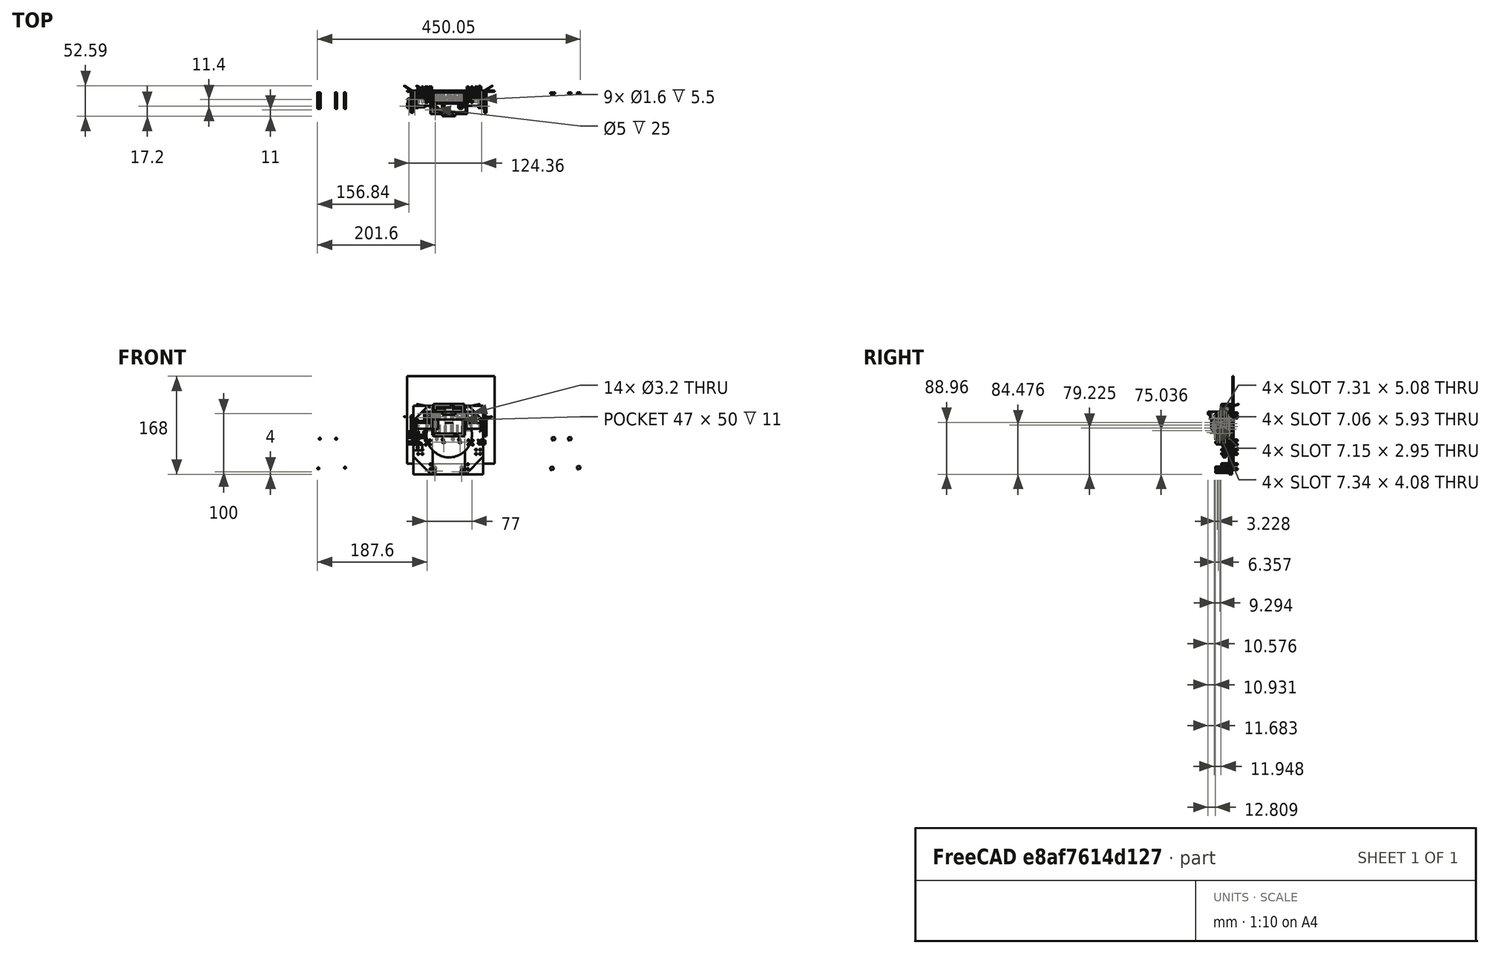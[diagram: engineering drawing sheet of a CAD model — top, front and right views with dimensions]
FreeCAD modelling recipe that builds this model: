
FCSTD DOCUMENT  (FreeCAD 0.17R13522 (Git))
Label: 5028.7 Blank Frank
License: All rights reserved
LicenseURL: http://en.wikipedia.org/wiki/All_rights_reserved
objects: Part::Cylinder×133, Part::Box×78, Part::Fuse×69, Part::Cut×66, Part::Feature×37, Part::MultiFuse×31, Part::Fillet×15, Part::Mirroring×14, Part::Chamfer×10, Part::Cone×9, Part::Compound×3, Part::Torus×2, App::DocumentObjectGroup×1
note: 467 computed .brp shape members not serialized (recipe doc carries the construction recipe); baked Part::Feature solids carry a one-line shape summary decoded from their .brp

FEATURE [Part::Cylinder] Cylinder
  Angle = 360
  AttacherType = Attacher::AttachEngine3D
  Height = 30
  Radius = 7
FEATURE [Part::Cylinder] Cylinder001
  Angle = 360
  AttacherType = Attacher::AttachEngine3D
  Height = 19
  Placement = pos=(0,0,30) rot=(0,0,1;0rad)
  Radius = 7
FEATURE [Part::Cylinder] Cylinder002
  Angle = 360
  AttacherType = Attacher::AttachEngine3D
  Height = 1.8
  Placement = pos=(0,0,49) rot=(0,0,1;0rad)
  Radius = 2.5
FEATURE [Part::Compound] Compound
  Links = -> [Cylinder,Cylinder002,Cylinder001]
FEATURE [Part::Cylinder] Cylinder003
  Angle = 360
  AttacherType = Attacher::AttachEngine3D
  Height = 30
  Radius = 7
FEATURE [Part::Cylinder] Cylinder004
  Angle = 360
  AttacherType = Attacher::AttachEngine3D
  Height = 19
  Placement = pos=(0,0,30) rot=(0,0,1;0rad)
  Radius = 7
FEATURE [Part::Cylinder] Cylinder005
  Angle = 360
  AttacherType = Attacher::AttachEngine3D
  Height = 1.8
  Placement = pos=(0,0,49) rot=(0,0,1;0rad)
  Radius = 2.5
FEATURE [Part::Compound] Compound001
  Links = -> [Cylinder003,Cylinder005,Cylinder004]
  Placement = pos=(14.5,0,50) rot=(1,0,0;3.14159rad)
FEATURE [Part::Cylinder] Cylinder006
  Angle = 360
  AttacherType = Attacher::AttachEngine3D
  Height = 30
  Radius = 7
FEATURE [Part::Cylinder] Cylinder007
  Angle = 360
  AttacherType = Attacher::AttachEngine3D
  Height = 19
  Placement = pos=(0,0,30) rot=(0,0,1;0rad)
  Radius = 7
FEATURE [Part::Cylinder] Cylinder008
  Angle = 360
  AttacherType = Attacher::AttachEngine3D
  Height = 1.8
  Placement = pos=(0,0,49) rot=(0,0,1;0rad)
  Radius = 2.5
FEATURE [Part::Compound] Compound002
  Links = -> [Cylinder006,Cylinder008,Cylinder007]
  Placement = pos=(29,0,0) rot=(0,0,1;0rad)
FEATURE [Part::Box] Box  label="Cube"
  AttacherType = Attacher::AttachEngine3D
  Height = 50
  Length = 47
  Placement = pos=(-9,-8,0) rot=(0,0,1;0rad)
  Width = 12
FEATURE [Part::Box] Box001  label="Cube001"
  AttacherType = Attacher::AttachEngine3D
  Height = 55
  Length = 53
  Placement = pos=(-12,-8,-2.5) rot=(0,0,1;0rad)
  Width = 11
FEATURE [Part::Cylinder] Cylinder009
  Angle = 360
  AttacherType = Attacher::AttachEngine3D
  Height = 50
  Radius = 7
FEATURE [Part::Cylinder] Cylinder010
  Angle = 360
  AttacherType = Attacher::AttachEngine3D
  Height = 50
  Placement = pos=(14.5,0,0) rot=(0,0,1;0rad)
  Radius = 7
FEATURE [Part::Cut] Cut
  Base = -> Box001
  Tool = -> Box
FEATURE [Part::Box] Box002  label="Cube002"
  AttacherType = Attacher::AttachEngine3D
  Height = 55
  Length = 53
  Placement = pos=(-12,3,-2.5) rot=(0,0,1;0rad)
  Width = 7
FEATURE [Part::Fuse] Fusion
  Base = -> Cut
  Tool = -> Box002
FEATURE [Part::Cut] Cut001  label="No idea why this is here...."
  Base = -> Fusion
  Tool = -> Cylinder009
FEATURE [Part::Cylinder] Cylinder011
  Angle = 360
  AttacherType = Attacher::AttachEngine3D
  Height = 50
  Placement = pos=(29,0,0) rot=(0,0,1;0rad)
  Radius = 7
FEATURE [Part::Box] Box003  label="Cube003"
  AttacherType = Attacher::AttachEngine3D
  Height = 5
  Length = 2
  Placement = pos=(28,-9,-2) rot=(0,0,1;0rad)
  Width = 12
FEATURE [Part::Box] Box004  label="Cube004"
  AttacherType = Attacher::AttachEngine3D
  Height = 5
  Length = 2
  Placement = pos=(18.5,-9,46) rot=(0,0,1;0rad)
  Width = 12
FEATURE [Part::Box] Box005  label="Cube005"
  AttacherType = Attacher::AttachEngine3D
  Height = 5
  Length = 2
  Placement = pos=(-2,-9,46) rot=(0,0,1;0rad)
  Width = 12
FEATURE [Part::Box] Box006  label="Cube006"
  AttacherType = Attacher::AttachEngine3D
  Height = 5
  Length = 3
  Placement = pos=(35,-9,-4) rot=(0,0,1;0rad)
  Width = 12
FEATURE [Part::Cut] Cut008
FEATURE [Part::Torus] Torus001
  Angle1 = -180
  Angle2 = 180
  Angle3 = 360
  AttacherType = Attacher::AttachEngine3D
  Placement = pos=(0,0,2) rot=(0,0,1;0rad)
  Radius1 = 19
  Radius2 = 1.5
FEATURE [Part::Cut] Cut009  label="wheel2"
  Base = -> Cut008
  Placement = pos=(75,-7,15) rot=(0,1,0;1.5708rad)
  Tool = -> Torus001
FEATURE [Part::Torus] Torus
  Angle1 = -180
  Angle2 = 180
  Angle3 = 360
  AttacherType = Attacher::AttachEngine3D
  Placement = pos=(0,0,2) rot=(0,0,1;0rad)
  Radius1 = 19
  Radius2 = 1.5
FEATURE [Part::Cut] Cut010
FEATURE [Part::Cut] Cut011  label="wheel1"
  Base = -> Cut010
  Placement = pos=(-51,-7,15) rot=(0,1,0;1.5708rad)
  Tool = -> Torus
FEATURE [Part::Fuse] Fusion003
FEATURE [Part::Cylinder] Cylinder012
  Angle = 360
  AttacherType = Attacher::AttachEngine3D
  Height = 10
  Placement = pos=(5,-4.5,0) rot=(0,1,0;1.5708rad)
  Radius = 0.8
FEATURE [Part::Fuse] Fusion048  label="right-motor001"
  Base = -> Cylinder012
  Placement = pos=(-51,-7,15) rot=(0,0,1;0rad)
  Tool = -> Fusion003
FEATURE [Part::Fuse] Fusion049
FEATURE [Part::Cylinder] Cylinder013
  Angle = 360
  AttacherType = Attacher::AttachEngine3D
  Height = 10
  Placement = pos=(5,-4.5,0) rot=(0,1,0;1.5708rad)
  Radius = 0.8
FEATURE [Part::Fuse] Fusion050  label="left-motor001"
  Base = -> Cylinder013
  Placement = pos=(79,-7,15) rot=(0,0,1;3.14159rad)
  Tool = -> Fusion049
FEATURE [Part::Box] Box007  label="Cube007"
  AttacherType = Attacher::AttachEngine3D
  Height = 5
  Length = 2
  Placement = pos=(37.5,-9,46) rot=(0,0,1;0rad)
  Width = 12
FEATURE [Part::Box] Box008  label="Cube008"
  AttacherType = Attacher::AttachEngine3D
  Height = 5
  Length = 2
  Placement = pos=(8,-9,-2) rot=(0,0,1;0rad)
  Width = 12
FEATURE [Part::Box] Box009  label="The Ground"
  AttacherType = Attacher::AttachEngine3D
  Height = 150
  Length = 150
  Placement = pos=(-57,11,-50) rot=(0,0,1;0rad)
  Width = 2
FEATURE [Part::Box] Box010  label="Motor Mount Left"
  AttacherType = Attacher::AttachEngine3D
  Height = 16
  Length = 4
  Placement = pos=(69,-13,7) rot=(0,0,1;0rad)
  Width = 20
FEATURE [Part::Box] Box011  label="Motor Mount Right"
  AttacherType = Attacher::AttachEngine3D
  Height = 16
  Length = 4
  Placement = pos=(-46,-13,7) rot=(0,0,1;0rad)
  Width = 20
FEATURE [Part::Box] Box012  label="Motor Support Right"
  AttacherType = Attacher::AttachEngine3D
  Height = 16
  Length = 10
  Placement = pos=(-25,-1,7) rot=(0,0,1;0rad)
  Width = 8
FEATURE [Part::Box] Box013  label="Motor Support Left"
  AttacherType = Attacher::AttachEngine3D
  Height = 16
  Length = 10
  Placement = pos=(43,-1,7) rot=(0,0,1;0rad)
  Width = 8
FEATURE [Part::Cylinder] Cylinder014
  Angle = 360
  AttacherType = Attacher::AttachEngine3D
  Height = 28
  Placement = pos=(40.7,0,-10.3) rot=(1,0,0;1.5708rad)
  Radius = 1.6
FEATURE [Part::Cylinder] Cylinder015
  Angle = 360
  AttacherType = Attacher::AttachEngine3D
  Height = 28
  Placement = pos=(-2.4,0,-59.8) rot=(1,0,0;1.5708rad)
  Radius = 1.6
FEATURE [Part::Cylinder] Cylinder016
  Angle = 360
  AttacherType = Attacher::AttachEngine3D
  Height = 28
  Placement = pos=(-5,0,-9) rot=(1,0,0;1.5708rad)
  Radius = 1.6
FEATURE [Part::Cylinder] Cylinder017
  Angle = 360
  AttacherType = Attacher::AttachEngine3D
  Height = 28
  Placement = pos=(25.5,0,-59.8) rot=(1,0,0;1.5708rad)
  Radius = 1.6
FEATURE [Part::Fuse] Fusion051
  Base = -> Cylinder015
  Tool = -> Cylinder016
FEATURE [Part::Fuse] Fusion052
  Base = -> Cylinder014
  Tool = -> Cylinder017
FEATURE [Part::Fuse] Fusion053  label="Screw holes on Arduino Duo"
  Base = -> Fusion051
  Tool = -> Fusion052
FEATURE [Part::Mirroring] Part__Mirroring  label="XXXXXScrew holes on Arduino Duo (Mirror #1)"
  Base = (0,0,0)
  Normal = (0,0,1)
  Placement = pos=(-204,10,-67) rot=(0,0,1;0rad)
  Source = -> Fusion053
FEATURE [Part::Box] Box014  label="Not used Cube"
  AttacherType = Attacher::AttachEngine3D
  Height = 10
  Length = 10
  Placement = pos=(-1,4,-5.85) rot=(0,0,1;0rad)
  Width = 10
FEATURE [Part::Box] Box015  label="Cube014 Arduino Support cube"
  AttacherType = Attacher::AttachEngine3D
  Height = 67
  Length = 55
  Placement = pos=(-13,5,-68) rot=(0,0,1;0rad)
  Width = 5
FEATURE [Part::Cylinder] Cylinder018
  Angle = 360
  AttacherType = Attacher::AttachEngine3D
  Height = 5
  Placement = pos=(15,0,0) rot=(1,0,0;1.5708rad)
  Radius = 39
FEATURE [Part::Cut] Cut014  label="M3 Nut"
  Base = -> Cut001
  Placement = pos=(-6.4,10,-7.2) rot=(1,0,0;1.5708rad)
  Tool = -> Cylinder001
FEATURE [Part::Cut] Cut015  label="M3 Nut001"
  Base = -> Cut001
  Placement = pos=(21.5,10,-7.2) rot=(1,0,0;1.5708rad)
  Tool = -> Cylinder001
FEATURE [Part::Cut] Cut016  label="M3 Nut002"
  Base = -> Cut001
  Placement = pos=(36.7,10,-56.7) rot=(1,0,0;1.5708rad)
  Tool = -> Cylinder001
FEATURE [Part::Cut] Cut017  label="M3 Nut003"
  Base = -> Cut001
  Placement = pos=(-9,10,-58) rot=(1,0,0;1.5708rad)
  Tool = -> Cylinder001
FEATURE [Part::Cut] Cut018
  Base = -> Cut
  Placement = pos=(-9,10,-58) rot=(1,0,0;1.5708rad)
  Tool = -> Box006
FEATURE [Part::Cut] Cut019
  Base = -> Cut
  Placement = pos=(36.7,10,-56.7) rot=(1,0,0;1.5708rad)
  Tool = -> Box006
FEATURE [Part::Cut] Cut020
  Base = -> Cut
  Placement = pos=(-6.4,10,-7.2) rot=(1,0,0;1.5708rad)
  Tool = -> Box006
FEATURE [Part::Cut] Cut021
  Base = -> Cut
  Placement = pos=(21.5,10,-7.2) rot=(1,0,0;1.5708rad)
  Tool = -> Box006
FEATURE [Part::MultiFuse] Fusion054  label="XXXXXHex Holes"
  Placement = pos=(200,0,0) rot=(0,0,1;0rad)
  Shapes = -> [Cut018,Cut021,Cut019,Cut020]
FEATURE [Part::Box] Box016  label="Cube015"
  AttacherType = Attacher::AttachEngine3D
  Height = 117
  Length = 33
  Placement = pos=(-46,7,-68) rot=(0,0,1;0rad)
  Width = 3
FEATURE [Part::Box] Box017  label="Cube016"
  AttacherType = Attacher::AttachEngine3D
  Height = 117
  Length = 31
  Placement = pos=(42,7,-68) rot=(0,0,1;0rad)
  Width = 3
FEATURE [Part::Cylinder] Cylinder019
  Angle = 360
  AttacherType = Attacher::AttachEngine3D
  Height = 28
  Placement = pos=(48,20,-10) rot=(1,0,0;1.5708rad)
  Radius = 1.6
FEATURE [Part::Cylinder] Cylinder020
  Angle = 360
  AttacherType = Attacher::AttachEngine3D
  Height = 28
  Placement = pos=(47,20,-51) rot=(1,0,0;1.5708rad)
  Radius = 1.6
FEATURE [Part::Cylinder] Cylinder021
  Angle = 360
  AttacherType = Attacher::AttachEngine3D
  Height = 28
  Placement = pos=(48,20,-17) rot=(1,0,0;1.5708rad)
  Radius = 1.6
FEATURE [Part::Cylinder] Cylinder022
  Angle = 360
  AttacherType = Attacher::AttachEngine3D
  Height = 28
  Placement = pos=(47,20,-59) rot=(1,0,0;1.5708rad)
  Radius = 1.6
FEATURE [Part::Cylinder] Cylinder023
  Angle = 360
  AttacherType = Attacher::AttachEngine3D
  Height = 28
  Placement = pos=(55,20,-17) rot=(1,0,0;1.5708rad)
  Radius = 1.6
FEATURE [Part::Cylinder] Cylinder024
  Angle = 360
  AttacherType = Attacher::AttachEngine3D
  Height = 28
  Placement = pos=(55,20,-10) rot=(1,0,0;1.5708rad)
  Radius = 1.6
FEATURE [Part::MultiFuse] Fusion055
  Shapes = -> [Cylinder021,Cylinder023,Cylinder024,Cylinder019]
FEATURE [Part::MultiFuse] Fusion056
  Placement = pos=(13,0,-16) rot=(0,0,1;0rad)
  Shapes = -> [Cylinder021,Cylinder023,Cylinder024,Cylinder019]
FEATURE [Part::MultiFuse] Fusion057  label="Mount holes top left"
  Placement = pos=(-1,0,46) rot=(0,0,1;0rad)
  Shapes = -> [Cylinder021,Cylinder023,Cylinder024,Cylinder019]
FEATURE [Part::MultiFuse] Fusion058  label="Mount holes top right"
  Placement = pos=(-71,0,46) rot=(0,0,1;0rad)
  Shapes = -> [Cylinder021,Cylinder023,Cylinder024,Cylinder019]
FEATURE [Part::MultiFuse] Fusion059
  Shapes = -> [Cylinder022,Cylinder020,Fusion055,Fusion056]
FEATURE [Part::Mirroring] Part__Mirroring001  label="Mount holes bottom right"
  Base = (0,0,0)
  Normal = (1,0,0)
  Placement = pos=(30,0,0) rot=(0,0,1;0rad)
  Source = -> Fusion059
FEATURE [Part::Cylinder] Cylinder025
  Angle = 360
  AttacherType = Attacher::AttachEngine3D
  Height = 28
  Placement = pos=(48,20,-10) rot=(1,0,0;1.5708rad)
  Radius = 1.6
FEATURE [Part::Cylinder] Cylinder026
  Angle = 360
  AttacherType = Attacher::AttachEngine3D
  Height = 28
  Placement = pos=(47,20,-51) rot=(1,0,0;1.5708rad)
  Radius = 1.6
FEATURE [Part::Cylinder] Cylinder027
  Angle = 360
  AttacherType = Attacher::AttachEngine3D
  Height = 28
  Placement = pos=(48,20,-17) rot=(1,0,0;1.5708rad)
  Radius = 1.6
FEATURE [Part::Cylinder] Cylinder028
  Angle = 360
  AttacherType = Attacher::AttachEngine3D
  Height = 28
  Placement = pos=(47,20,-59) rot=(1,0,0;1.5708rad)
  Radius = 1.6
FEATURE [Part::Cylinder] Cylinder029
  Angle = 360
  AttacherType = Attacher::AttachEngine3D
  Height = 28
  Placement = pos=(55,20,-17) rot=(1,0,0;1.5708rad)
  Radius = 1.6
FEATURE [Part::Cylinder] Cylinder030
  Angle = 360
  AttacherType = Attacher::AttachEngine3D
  Height = 28
  Placement = pos=(55,20,-10) rot=(1,0,0;1.5708rad)
  Radius = 1.6
FEATURE [Part::MultiFuse] Fusion060
  Shapes = -> [Cylinder027,Cylinder029,Cylinder030,Cylinder025]
FEATURE [Part::MultiFuse] Fusion061
  Placement = pos=(13,0,-16) rot=(0,0,1;0rad)
  Shapes = -> [Cylinder027,Cylinder029,Cylinder030,Cylinder025]
FEATURE [Part::MultiFuse] Fusion062  label="Mount holes bottom left"
  Shapes = -> [Cylinder028,Cylinder026,Fusion060,Fusion061]
FEATURE [Part::Cylinder] Cylinder031  label="Cylinder127"
  Angle = 360
  AttacherType = Attacher::AttachEngine3D
  Height = 10
  Placement = pos=(0,18,29) rot=(0,0,1;0rad)
  Radius = 2.25
FEATURE [Part::Cylinder] Cylinder032  label="Cylinder128"
  Angle = 360
  AttacherType = Attacher::AttachEngine3D
  Height = 10
  Placement = pos=(4.5,18,32) rot=(0,0,1;0rad)
  Radius = 1
FEATURE [Part::Cylinder] Cylinder033  label="Cylinder129"
  Angle = 360
  AttacherType = Attacher::AttachEngine3D
  Height = 10
  Placement = pos=(-4.5,18,32) rot=(0,0,1;0rad)
  Radius = 1
FEATURE [Part::Fuse] Fusion009  label="Mounting Screw Holes"
  Base = -> Cylinder032
  Tool = -> Cylinder033
FEATURE [Part::Fuse] Fusion071  label="Motor Holes Left"
  Base = -> Cylinder031
  Placement = pos=(37,-7,-3) rot=(0.57735,0.57735,0.57735;2.0944rad)
  Tool = -> Fusion009
FEATURE [Part::Cylinder] Cylinder034  label="Cylinder130"
  Angle = 360
  AttacherType = Attacher::AttachEngine3D
  Height = 10
  Placement = pos=(0,18,29) rot=(0,0,1;0rad)
  Radius = 2.25
FEATURE [Part::Cylinder] Cylinder035  label="Cylinder131"
  Angle = 360
  AttacherType = Attacher::AttachEngine3D
  Height = 10
  Placement = pos=(4.5,18,32) rot=(0,0,1;0rad)
  Radius = 1
FEATURE [Part::Cylinder] Cylinder036  label="Cylinder132"
  Angle = 360
  AttacherType = Attacher::AttachEngine3D
  Height = 10
  Placement = pos=(-4.5,18,32) rot=(0,0,1;0rad)
  Radius = 1
FEATURE [Part::Fuse] Fusion072  label="Mounting Screw Holes001"
  Base = -> Cylinder035
  Tool = -> Cylinder036
FEATURE [Part::Fuse] Fusion073  label="Motor Holes Right"
  Base = -> Cylinder034
  Placement = pos=(-79,-7,-3) rot=(0.57735,0.57735,0.57735;2.0944rad)
  Tool = -> Fusion072
FEATURE [Part::Cylinder] Cylinder037  label="Cylinder133"
  Angle = 360
  AttacherType = Attacher::AttachEngine3D
  Height = 28
  Placement = pos=(40.7,0,-10.3) rot=(1,0,0;1.5708rad)
  Radius = 1.6
FEATURE [Part::Cylinder] Cylinder038  label="Cylinder134"
  Angle = 360
  AttacherType = Attacher::AttachEngine3D
  Height = 28
  Placement = pos=(-2.4,0,-59.8) rot=(1,0,0;1.5708rad)
  Radius = 1.6
FEATURE [Part::Cylinder] Cylinder039  label="Cylinder135"
  Angle = 360
  AttacherType = Attacher::AttachEngine3D
  Height = 28
  Placement = pos=(-5,0,-9) rot=(1,0,0;1.5708rad)
  Radius = 1.6
FEATURE [Part::Cylinder] Cylinder040  label="Cylinder136"
  Angle = 360
  AttacherType = Attacher::AttachEngine3D
  Height = 28
  Placement = pos=(25.5,0,-59.8) rot=(1,0,0;1.5708rad)
  Radius = 1.6
FEATURE [Part::Fuse] Fusion074
  Base = -> Cylinder038
  Tool = -> Cylinder039
FEATURE [Part::Fuse] Fusion075
  Base = -> Cylinder037
  Tool = -> Cylinder040
FEATURE [Part::Fuse] Fusion076  label="Screw holes on Arduino Duo001"
  Base = -> Fusion074
  Tool = -> Fusion075
FEATURE [Part::Mirroring] Part__Mirroring002  label="Screw holes on Arduino Duo (Mirror #1)001"
  Base = (0,0,0)
  Normal = (0,0,1)
  Placement = pos=(-4,10,-67) rot=(0,0,1;0rad)
  Source = -> Fusion076
FEATURE [Part::Mirroring] Part__Mirroring003  label="Screw holes on Arduino Duo (Mirror #1)001 (Mirror #4)"
  Base = (0,0,0)
  Normal = (1,0,0)
  Placement = pos=(27,0,-6) rot=(0,0,1;0rad)
  Source = -> Part__Mirroring002
FEATURE [Part::Box] Box018  label="Cube017"
  AttacherType = Attacher::AttachEngine3D
  Height = 50
  Length = 47
  Placement = pos=(-9,-8,0) rot=(0,0,1;0rad)
  Width = 12
FEATURE [Part::Box] Box019  label="Cube018"
  AttacherType = Attacher::AttachEngine3D
  Height = 55
  Length = 53
  Placement = pos=(-12,-8,-2.5) rot=(0,0,1;0rad)
  Width = 11
FEATURE [Part::Cut] Cut031
  Base = -> Box019
  Tool = -> Box018
FEATURE [Part::Box] Box020  label="Cube019"
  AttacherType = Attacher::AttachEngine3D
  Height = 5
  Length = 3
  Placement = pos=(35,-9,-4) rot=(0,0,1;0rad)
  Width = 12
FEATURE [Part::Cut] Cut032
  Base = -> Cut031
  Placement = pos=(-9,10,-58) rot=(1,0,0;1.5708rad)
  Tool = -> Box020
FEATURE [Part::Cut] Cut033
  Base = -> Cut031
  Placement = pos=(36.7,10,-56.7) rot=(1,0,0;1.5708rad)
  Tool = -> Box020
FEATURE [Part::Cut] Cut034
  Base = -> Cut031
  Placement = pos=(-6.4,10,-7.2) rot=(1,0,0;1.5708rad)
  Tool = -> Box020
FEATURE [Part::Cut] Cut035
  Base = -> Cut031
  Placement = pos=(21.5,10,-7.2) rot=(1,0,0;1.5708rad)
  Tool = -> Box020
FEATURE [Part::MultiFuse] Fusion077
  Shapes = -> [Cut032,Cut035,Cut033,Cut034]
FEATURE [Part::Mirroring] Part__Mirroring004  label="Hex Holes"
  Base = (0,0,0)
  Normal = (1,0,0)
  Placement = pos=(27,0,-6) rot=(0,0,1;0rad)
  Source = -> Fusion077
FEATURE [Part::Box] Box021  label="Cube020"
  AttacherType = Attacher::AttachEngine3D
  Height = 13
  Length = 63
  Placement = pos=(-17,-27,26) rot=(0,0,1;0rad)
  Width = 34
FEATURE [Part::Box] Box022  label="Cube021"
  AttacherType = Attacher::AttachEngine3D
  Height = 13
  Length = 12
  Placement = pos=(45,4,26) rot=(0,0,1;0rad)
  Width = 3
FEATURE [Part::Box] Box023  label="Cube022"
  AttacherType = Attacher::AttachEngine3D
  Height = 13
  Length = 12
  Placement = pos=(-28,4,26) rot=(0,0,1;0rad)
  Width = 3
FEATURE [Part::Box] Box024  label="Cube023"
  AttacherType = Attacher::AttachEngine3D
  Height = 13
  Length = 57
  Placement = pos=(-14,-24,26) rot=(0,0,1;0rad)
  Width = 31
FEATURE [Part::Cylinder] Cylinder041  label="Cylinder137"
  Angle = 360
  AttacherType = Attacher::AttachEngine3D
  Height = 28
  Placement = pos=(54,20,29) rot=(1,0,0;1.5708rad)
  Radius = 1.6
FEATURE [Part::Cylinder] Cylinder042  label="Cylinder138"
  Angle = 360
  AttacherType = Attacher::AttachEngine3D
  Height = 28
  Placement = pos=(54,20,36) rot=(1,0,0;1.5708rad)
  Radius = 1.6
FEATURE [Part::Cylinder] Cylinder043  label="Cylinder139"
  Angle = 360
  AttacherType = Attacher::AttachEngine3D
  Height = 28
  Placement = pos=(-23,20,29) rot=(1,0,0;1.5708rad)
  Radius = 1.6
FEATURE [Part::Cylinder] Cylinder044  label="Cylinder140"
  Angle = 360
  AttacherType = Attacher::AttachEngine3D
  Height = 28
  Placement = pos=(-23,20,36) rot=(1,0,0;1.5708rad)
  Radius = 1.6
FEATURE [Part::Cylinder] Cylinder045  label="Cylinder141"
  Angle = 360
  AttacherType = Attacher::AttachEngine3D
  Height = 10
  Placement = pos=(36,-17.25,32.5) rot=(0,1,0;1.5708rad)
  Radius = 2.5
FEATURE [Part::Cut] Cut037
  Base = -> Box021
  Tool = -> Box024
FEATURE [Part::Cut] Cut038
  Base = -> Cut037
  Tool = -> Cylinder045
FEATURE [Part::Box] Box025  label="Cube024"
  AttacherType = Attacher::AttachEngine3D
  Height = 5
  Length = 22
  Placement = pos=(3.5,-31,34) rot=(0,0,1;0rad)
  Width = 4
FEATURE [Part::Cylinder] Cylinder046  label="Cylinder142"
  Angle = 360
  AttacherType = Attacher::AttachEngine3D
  Height = 10
  Placement = pos=(20.75,-29,30) rot=(0,0,1;0rad)
  Radius = 0.85
FEATURE [Part::Cylinder] Cylinder047  label="Cylinder143"
  Angle = 360
  AttacherType = Attacher::AttachEngine3D
  Height = 10
  Placement = pos=(8.25,-29,40) rot=(1,0,0;3.14159rad)
  Radius = 0.85
FEATURE [Part::Fuse] Fusion078
  Base = -> Cylinder046
  Tool = -> Cylinder047
FEATURE [Part::Cut] Cut039
  Base = -> Box025
  Tool = -> Fusion078
FEATURE [Part::Fuse] Fusion079
  Base = -> Cut038
  Tool = -> Cut039
FEATURE [Part::Fuse] Fusion080
  Base = -> Cylinder043
  Tool = -> Cylinder044
FEATURE [Part::Fuse] Fusion081
  Base = -> Cylinder041
  Tool = -> Cylinder042
FEATURE [Part::Fuse] Fusion082
  Base = -> Box023
  Tool = -> Fusion079
FEATURE [Part::Fuse] Fusion083
  Base = -> Box022
  Tool = -> Fusion082
FEATURE [Part::Cut] Cut040
  Base = -> Fusion083
  Tool = -> Fusion081
FEATURE [Part::Cut] Cut041  label="Switch Bracket"
  Base = -> Cut040
  Tool = -> Fusion080
FEATURE [Part::Cylinder] Cylinder048  label="Cylinder144"
  Angle = 360
  AttacherType = Attacher::AttachEngine3D
  Height = 28
  Placement = pos=(-23,20,29) rot=(1,0,0;1.5708rad)
  Radius = 1.6
FEATURE [Part::Cylinder] Cylinder049  label="Cylinder145"
  Angle = 360
  AttacherType = Attacher::AttachEngine3D
  Height = 28
  Placement = pos=(-23,20,36) rot=(1,0,0;1.5708rad)
  Radius = 1.6
FEATURE [Part::Fuse] Fusion084
  Base = -> Cylinder048
  Placement = pos=(1,0,0) rot=(0,0,1;0rad)
  Tool = -> Cylinder049
FEATURE [Part::Cylinder] Cylinder050  label="Cylinder146"
  Angle = 360
  AttacherType = Attacher::AttachEngine3D
  Height = 28
  Placement = pos=(-23,20,29) rot=(1,0,0;1.5708rad)
  Radius = 1.6
FEATURE [Part::Cylinder] Cylinder051  label="Cylinder147"
  Angle = 360
  AttacherType = Attacher::AttachEngine3D
  Height = 28
  Placement = pos=(-23,20,36) rot=(1,0,0;1.5708rad)
  Radius = 1.6
FEATURE [Part::Fuse] Fusion085
  Base = -> Cylinder050
  Placement = pos=(-1,0,0) rot=(0,0,1;0rad)
  Tool = -> Cylinder051
FEATURE [Part::Cut] Cut042
  Base = -> Cut041
  Tool = -> Fusion084
FEATURE [Part::Cut] Cut043  label="Switch Bracket001"
  Base = -> Cut042
  Tool = -> Fusion085
FEATURE [Part::Cylinder] Cylinder052  label="Cylinder148"
  Angle = 360
  AttacherType = Attacher::AttachEngine3D
  Height = 42
  Radius = 5.15
FEATURE [Part::Cylinder] Cylinder053  label="Cylinder149"
  Angle = 360
  AttacherType = Attacher::AttachEngine3D
  Height = 1.6
  Placement = pos=(0,0,42) rot=(0,0,1;0rad)
  Radius = 1.65
FEATURE [Part::Fuse] Fusion086
  Base = -> Cylinder052
  Placement = pos=(2,0,0) rot=(0,0,1;0rad)
  Tool = -> Cylinder053
FEATURE [Part::Cylinder] Cylinder054  label="Cylinder150"
  Angle = 360
  AttacherType = Attacher::AttachEngine3D
  Height = 42
  Radius = 4.8
FEATURE [Part::Cylinder] Cylinder055  label="Cylinder151"
  Angle = 360
  AttacherType = Attacher::AttachEngine3D
  Height = 1.6
  Placement = pos=(0,0,42) rot=(0,0,1;0rad)
  Radius = 1.65
FEATURE [Part::Fuse] Fusion087
  Base = -> Cylinder054
  Placement = pos=(12,0,0) rot=(0,0,1;0rad)
  Tool = -> Cylinder055
FEATURE [Part::Cylinder] Cylinder056  label="Cylinder152"
  Angle = 360
  AttacherType = Attacher::AttachEngine3D
  Height = 42
  Radius = 4.8
FEATURE [Part::Cylinder] Cylinder057  label="Cylinder153"
  Angle = 360
  AttacherType = Attacher::AttachEngine3D
  Height = 1.6
  Placement = pos=(0,0,42) rot=(0,0,1;0rad)
  Radius = 1.65
FEATURE [Part::Fuse] Fusion088
  Base = -> Cylinder056
  Placement = pos=(22,0,0) rot=(0,0,1;0rad)
  Tool = -> Cylinder057
FEATURE [Part::Cylinder] Cylinder058  label="Cylinder154"
  Angle = 360
  AttacherType = Attacher::AttachEngine3D
  Height = 42
  Radius = 4.8
FEATURE [Part::Cylinder] Cylinder059  label="Cylinder155"
  Angle = 360
  AttacherType = Attacher::AttachEngine3D
  Height = 1.6
  Placement = pos=(0,0,42) rot=(0,0,1;0rad)
  Radius = 1.65
FEATURE [Part::Fuse] Fusion089
  Base = -> Cylinder058
  Placement = pos=(32,0,0) rot=(0,0,1;0rad)
  Tool = -> Cylinder059
FEATURE [Part::Cylinder] Cylinder060  label="Cylinder156"
  Angle = 360
  AttacherType = Attacher::AttachEngine3D
  Height = 42
  Radius = 5.15
FEATURE [Part::Cylinder] Cylinder061  label="Cylinder157"
  Angle = 360
  AttacherType = Attacher::AttachEngine3D
  Height = 1.6
  Placement = pos=(0,0,42) rot=(0,0,1;0rad)
  Radius = 1.65
FEATURE [Part::Fuse] Fusion093
  Base = -> Cylinder060
  Placement = pos=(-8,0,0) rot=(0,0,1;0rad)
  Tool = -> Cylinder061
FEATURE [Part::MultiFuse] Fusion094  label="AAA Batts"
  Placement = pos=(2.5,0,2) rot=(0,0,1;0rad)
  Shapes = -> [Fusion093,Fusion086,Fusion087,Fusion088,Fusion089]
FEATURE [Part::Cylinder] Cylinder062  label="Cylinder158"
  Angle = 360
  AttacherType = Attacher::AttachEngine3D
  Height = 10
  Radius = 17
FEATURE [Part::Cylinder] Cylinder063  label="Cylinder159"
  Angle = 360
  AttacherType = Attacher::AttachEngine3D
  Height = 16
  Placement = pos=(0,0,-4) rot=(0,0,1;0rad)
  Radius = 10
FEATURE [Part::Cut] Cut044
  Base = -> Cylinder062
  Tool = -> Cylinder063
FEATURE [Part::Box] Box026  label="Cube025"
  AttacherType = Attacher::AttachEngine3D
  Height = 20
  Length = 18
  Placement = pos=(0,0,-5) rot=(0,0,1;0rad)
  Width = 20
FEATURE [Part::Box] Box027  label="Cube026"
  AttacherType = Attacher::AttachEngine3D
  Height = 20
  Length = 10
  Placement = pos=(0,0,-5) rot=(0,0,1;0.174533rad)
  Width = 20
FEATURE [Part::Cut] Cut045
  Base = -> Box027
  Tool = -> Box026
FEATURE [Part::Feature] Cut045001
  Placement = pos=(0,0,0) rot=(0,0,1;0.349066rad)
  shape: bbox 10 x 22.32 x 20 mm, 7 faces (baked)
FEATURE [Part::Feature] Cut045002
  Placement = pos=(0,0,0) rot=(0,0,1;0.698132rad)
  shape: bbox 15.32 x 20.52 x 20 mm, 7 faces (baked)
FEATURE [Part::Feature] Cut045003
  Placement = pos=(0,0,0) rot=(0,0,1;1.0472rad)
  shape: bbox 18.79 x 16.24 x 20 mm, 7 faces (baked)
FEATURE [Part::Feature] Cut045004
  Placement = pos=(0,0,0) rot=(0,0,1;1.39626rad)
  shape: bbox 20 x 10 x 20 mm, 7 faces (baked)
FEATURE [Part::Feature] Cut045005
  Placement = pos=(0,0,0) rot=(0,0,1;1.74533rad)
  shape: bbox 22.21 x 9.894 x 20 mm, 7 faces (baked)
FEATURE [Part::Feature] Cut045006
  Placement = pos=(0,0,0) rot=(0,0,1;2.0944rad)
  shape: bbox 21.75 x 12.86 x 20 mm, 7 faces (baked)
FEATURE [Part::Feature] Cut045007
  Placement = pos=(0,0,0) rot=(0,0,1;2.44346rad)
  shape: bbox 18.66 x 17.32 x 20 mm, 7 faces (baked)
FEATURE [Part::Feature] Cut045008
  Placement = pos=(0,0,0) rot=(0,0,1;2.79253rad)
  shape: bbox 13.32 x 19.7 x 20 mm, 7 faces (baked)
FEATURE [Part::Feature] Cut045009
  Placement = pos=(0,0,0) rot=(0,0,1;3.14159rad)
  shape: bbox 10.1 x 21.43 x 20 mm, 7 faces (baked)
FEATURE [Part::Feature] Cut045010
  Placement = pos=(0,0,0) rot=(0,0,1;3.49066rad)
  shape: bbox 10 x 22.32 x 20 mm, 7 faces (baked)
FEATURE [Part::Feature] Cut045011
  Placement = pos=(0,0,0) rot=(0,0,1;3.83972rad)
  shape: bbox 15.32 x 20.52 x 20 mm, 7 faces (baked)
FEATURE [Part::Feature] Cut045012
  Placement = pos=(0,0,0) rot=(0,0,1;4.18879rad)
  shape: bbox 18.79 x 16.24 x 20 mm, 7 faces (baked)
FEATURE [Part::Feature] Cut045013
  Placement = pos=(0,0,0) rot=(0,0,-1;1.74533rad)
  shape: bbox 20 x 10 x 20 mm, 7 faces (baked)
FEATURE [Part::Feature] Cut045014
  Placement = pos=(0,0,0) rot=(0,0,-1;1.39626rad)
  shape: bbox 22.21 x 9.894 x 20 mm, 7 faces (baked)
FEATURE [Part::Feature] Cut045015
  Placement = pos=(0,0,0) rot=(0,0,-1;1.0472rad)
  shape: bbox 21.75 x 12.86 x 20 mm, 7 faces (baked)
FEATURE [Part::Feature] Cut045016
  Placement = pos=(0,0,0) rot=(0,0,-1;0.698132rad)
  shape: bbox 18.66 x 17.32 x 20 mm, 7 faces (baked)
FEATURE [Part::Feature] Cut045017
  Placement = pos=(0,0,0) rot=(0,0,-1;0.349066rad)
  shape: bbox 13.32 x 19.7 x 20 mm, 7 faces (baked)
FEATURE [Part::MultiFuse] Fusion095
  Shapes = -> [Cut045001,Cut045008,Cut045010,Cut045009,Cut045005,Cut045003,Cut045006,Cut045002,Cut045004,Cut045007,Cut045016,Cut045017,Cut045011,Cut045012,Cut045013,Cut045014,Cut045015,Cut045]
FEATURE [Part::Cut] Cut045018
  Base = -> Cut044
  Placement = pos=(72,-7,15) rot=(0,1,0;1.5708rad)
  Tool = -> Fusion095
FEATURE [Part::Cut] Cut045019  label="Wheel with Spokes AB"
  Base = -> Cut009
  Tool = -> Cut045018
FEATURE [Part::Box] Box028  label="Cube027"
  AttacherType = Attacher::AttachEngine3D
  Height = 5
  Length = 2
  Placement = pos=(37.5,-9,-2) rot=(0,0,1;0rad)
  Width = 12
FEATURE [Part::Box] Box029  label="Cube028"
  AttacherType = Attacher::AttachEngine3D
  Height = 50
  Length = 47
  Placement = pos=(-9,-8,0) rot=(0,0,1;0rad)
  Width = 12
FEATURE [Part::Box] Box030  label="Cube029"
  AttacherType = Attacher::AttachEngine3D
  Height = 55
  Length = 53
  Placement = pos=(-12,-8,-2.5) rot=(0,0,1;0rad)
  Width = 11
FEATURE [Part::Cylinder] Cylinder064  label="Cylinder160"
  Angle = 360
  AttacherType = Attacher::AttachEngine3D
  Height = 50
  Radius = 7
FEATURE [Part::Cut] Cut045020
  Base = -> Box030
  Tool = -> Box029
FEATURE [Part::Box] Box031  label="Cube030"
  AttacherType = Attacher::AttachEngine3D
  Height = 55
  Length = 53
  Placement = pos=(-12,3,-2.5) rot=(0,0,1;0rad)
  Width = 7
FEATURE [Part::Fuse] Fusion096
  Base = -> Cut045020
  Tool = -> Box031
FEATURE [Part::Box] Box032  label="Battery Base"
  AttacherType = Attacher::AttachEngine3D
  Height = 50
  Length = 56
  Placement = pos=(-14,3,-1) rot=(0,0,1;0rad)
  Width = 7
FEATURE [Part::Box] Box033  label="Cube031"
  AttacherType = Attacher::AttachEngine3D
  Height = 30
  Length = 10
  Placement = pos=(-14,-25,9) rot=(0,0,1;0rad)
  Width = 10
FEATURE [Part::Cylinder] Cylinder065  label="Cylinder161"
  Angle = 360
  AttacherType = Attacher::AttachEngine3D
  Height = 43.5
  Placement = pos=(4,0,2) rot=(0,0,1;0rad)
  Radius = 4.8
FEATURE [Part::Cylinder] Cylinder066  label="Cylinder162"
  Angle = 360
  AttacherType = Attacher::AttachEngine3D
  Height = 1.6
  Placement = pos=(4,0,44) rot=(0,0,1;0rad)
  Radius = 1.65
FEATURE [Part::Fuse] Fusion097
  Base = -> Cylinder065
  Tool = -> Cylinder066
FEATURE [Part::Cylinder] Cylinder067  label="Cylinder163"
  Angle = 360
  AttacherType = Attacher::AttachEngine3D
  Height = 43.5
  Placement = pos=(14,0,2) rot=(0,0,1;0rad)
  Radius = 4.8
FEATURE [Part::Cylinder] Cylinder068  label="Cylinder164"
  Angle = 360
  AttacherType = Attacher::AttachEngine3D
  Height = 1.6
  Placement = pos=(14,0,44) rot=(0,0,1;0rad)
  Radius = 1.65
FEATURE [Part::Fuse] Fusion098
  Base = -> Cylinder067
  Tool = -> Cylinder068
FEATURE [Part::Cylinder] Cylinder069  label="Cylinder165"
  Angle = 360
  AttacherType = Attacher::AttachEngine3D
  Height = 43.5
  Placement = pos=(24,0,2) rot=(0,0,1;0rad)
  Radius = 4.8
FEATURE [Part::Cylinder] Cylinder070  label="Cylinder166"
  Angle = 360
  AttacherType = Attacher::AttachEngine3D
  Height = 1.6
  Placement = pos=(24,0,44) rot=(0,0,1;0rad)
  Radius = 1.65
FEATURE [Part::Fuse] Fusion099
  Base = -> Cylinder069
  Tool = -> Cylinder070
FEATURE [Part::Cylinder] Cylinder071  label="Cylinder167"
  Angle = 360
  AttacherType = Attacher::AttachEngine3D
  Height = 43.5
  Placement = pos=(34,0,2) rot=(0,0,1;0rad)
  Radius = 4.8
FEATURE [Part::Cylinder] Cylinder072  label="Cylinder168"
  Angle = 360
  AttacherType = Attacher::AttachEngine3D
  Height = 1.6
  Placement = pos=(34,0,44) rot=(0,0,1;0rad)
  Radius = 1.65
FEATURE [Part::Fuse] Fusion100
  Base = -> Cylinder071
  Tool = -> Cylinder072
FEATURE [Part::Cylinder] Cylinder073  label="Cylinder169"
  Angle = 360
  AttacherType = Attacher::AttachEngine3D
  Height = 43.5
  Placement = pos=(-6,0,2) rot=(0,0,1;0rad)
  Radius = 4.8
FEATURE [Part::Cylinder] Cylinder074  label="Cylinder170"
  Angle = 360
  AttacherType = Attacher::AttachEngine3D
  Height = 1.6
  Placement = pos=(-6,0,44) rot=(0,0,1;0rad)
  Radius = 1.65
FEATURE [Part::Fuse] Fusion101
  Base = -> Cylinder073
  Tool = -> Cylinder074
FEATURE [Part::MultiFuse] Fusion102  label="AAA Batts001"
  Shapes = -> [Fusion101,Fusion097,Fusion098,Fusion099,Fusion100]
FEATURE [Part::Cylinder] Cylinder075  label="Cylinder171"
  Angle = 360
  AttacherType = Attacher::AttachEngine3D
  Height = 10
  Placement = pos=(-9,-20,4) rot=(0,0,1;0rad)
  Radius = 2.75
FEATURE [Part::Cylinder] Cylinder076  label="Cylinder172"
  Angle = 360
  AttacherType = Attacher::AttachEngine3D
  Height = 27
  Placement = pos=(-9,-20,14) rot=(0,0,1;0rad)
  Radius = 2.5
FEATURE [Part::Fuse] Fusion103  label="phototransistor hole"
  Base = -> Cylinder075
  Tool = -> Cylinder076
FEATURE [Part::Cut] Cut045021  label="Phototransistor holder"
  Base = -> Box033
  Tool = -> Fusion103
FEATURE [Part::Fuse] Fusion104  label="Switch Mount with phototransistor hole"
  Base = -> Cut043
  Tool = -> Cut045021
FEATURE [Part::Cut] Cut045022
  Base = -> Box032
  Tool = -> Fusion102
FEATURE [Part::Box] Box034  label="Cube032"
  AttacherType = Attacher::AttachEngine3D
  Height = 2.5
  Length = 55
  Placement = pos=(-13,-9,-1) rot=(0,0,1;0rad)
  Width = 12
FEATURE [Part::Box] Box035  label="Cube033"
  AttacherType = Attacher::AttachEngine3D
  Height = 2.5
  Length = 55
  Placement = pos=(-13,-9,46.5) rot=(0,0,1;0rad)
  Width = 12
FEATURE [Part::Box] Box036  label="Cube034"
  AttacherType = Attacher::AttachEngine3D
  Height = 50
  Length = 2
  Placement = pos=(-14,-9,-1) rot=(0,0,1;0rad)
  Width = 12
FEATURE [Part::Box] Box037  label="Cube035"
  AttacherType = Attacher::AttachEngine3D
  Height = 50
  Length = 2
  Placement = pos=(40,-9,-1) rot=(0,0,1;0rad)
  Width = 12
FEATURE [Part::MultiFuse] Fusion105
  Shapes = -> [Box034,Box036,Box037,Box035]
FEATURE [Part::Box] Box038  label="Cube036"
  AttacherType = Attacher::AttachEngine3D
  Height = 5
  Length = 2
  Placement = pos=(-10.5,-9,46) rot=(0,0,1;0rad)
  Width = 12
FEATURE [Part::Box] Box039  label="Cube037"
  AttacherType = Attacher::AttachEngine3D
  Height = 5
  Length = 2
  Placement = pos=(-10.5,-9,-2) rot=(0,0,1;0rad)
  Width = 12
FEATURE [Part::MultiFuse] Fusion106
  Shapes = -> [Box039,Box038,Box028,Box007]
FEATURE [Part::MultiFuse] Fusion107
  Shapes = -> [Box003,Box004,Box005,Box008]
FEATURE [Part::Cut] Cut045023
  Base = -> Fusion105
  Tool = -> Fusion106
FEATURE [Part::Cut] Cut045024
  Base = -> Cut045023
  Tool = -> Fusion107
FEATURE [Part::Box] Box040  label="Cube038"
  AttacherType = Attacher::AttachEngine3D
  Height = 1.6
  Length = 30
  Placement = pos=(-56,-15.5,-6) rot=(0,0,1;0rad)
  Width = 15
FEATURE [Part::Box] Box041  label="Cube039"
  AttacherType = Attacher::AttachEngine3D
  Height = 10
  Length = 14
  Placement = pos=(-56,-10.5,-4.5) rot=(0,0,1;0rad)
  Width = 6
FEATURE [Part::Box] Box042  label="Cube040"
  AttacherType = Attacher::AttachEngine3D
  Height = 10
  Length = 5.3
  Placement = pos=(-51.7,-11.5,-4.5) rot=(0,0,1;0rad)
  Width = 8
FEATURE [Part::Cut] Cut045025
  Base = -> Box041
  Tool = -> Box042
FEATURE [Part::Fuse] Fusion108  label="Spoke Sensor PCB"
  Base = -> Box040
  Tool = -> Cut045025
FEATURE [Part::Cylinder] Cylinder077  label="Cylinder173"
  Angle = 360
  AttacherType = Attacher::AttachEngine3D
  Height = 14.5
  Placement = pos=(-43.6,-2.4,-9) rot=(0,0,1;0rad)
  Radius = 0.8
FEATURE [Part::Cylinder] Cylinder078  label="Cylinder174"
  Angle = 360
  AttacherType = Attacher::AttachEngine3D
  Height = 14.5
  Placement = pos=(-43.6,-13.8,-9) rot=(0,0,1;0rad)
  Radius = 0.8
FEATURE [Part::Fuse] Fusion109
  Base = -> Cylinder077
  Tool = -> Cylinder078
FEATURE [Part::Cut] Cut045026  label="Spoke Sensor PCB001"
  Base = -> Fusion108
  Tool = -> Fusion109
FEATURE [Part::Cylinder] Cylinder079  label="Cylinder175"
  Angle = 360
  AttacherType = Attacher::AttachEngine3D
  Height = 14.5
  Placement = pos=(-43.6,-2.4,-18) rot=(0,0,1;0rad)
  Radius = 0.8
FEATURE [Part::Cylinder] Cylinder080  label="Cylinder176"
  Angle = 360
  AttacherType = Attacher::AttachEngine3D
  Height = 14.5
  Placement = pos=(-43.6,-13.8,-18) rot=(0,0,1;0rad)
  Radius = 0.8
FEATURE [Part::Fuse] Fusion110  label="Batt Holder"
  Base = -> Cut045022
  Tool = -> Cut045024
FEATURE [Part::Box] Box043  label="Cube041"
  AttacherType = Attacher::AttachEngine3D
  Height = 4
  Length = 12
  Placement = pos=(-50,-16.75,-17) rot=(0,0,1;0rad)
  Width = 23.75
FEATURE [Part::Cone] Cone
  Angle = 360
  AttacherType = Attacher::AttachEngine3D
  Height = 1.5
  Placement = pos=(-43.6,-2.4,-13) rot=(0,0,1;0rad)
  Radius1 = 2.75
  Radius2 = 1.25
FEATURE [Part::Cone] Cone001
  Angle = 360
  AttacherType = Attacher::AttachEngine3D
  Height = 1.5
  Placement = pos=(-43.6,-13.8,-13) rot=(0,0,1;0rad)
  Radius1 = 2.75
  Radius2 = 1.25
FEATURE [Part::Fuse] Fusion111
  Base = -> Cone
  Tool = -> Cone001
FEATURE [Part::Fuse] Fusion113
  Base = -> Cylinder079
  Tool = -> Cylinder080
FEATURE [Part::Cylinder] Cylinder081  label="Cylinder177"
  Angle = 360
  AttacherType = Attacher::AttachEngine3D
  Height = 14.5
  Placement = pos=(-43.6,-2.4,-18) rot=(0,0,1;0rad)
  Radius = 0.8
FEATURE [Part::Cylinder] Cylinder082  label="Cylinder178"
  Angle = 360
  AttacherType = Attacher::AttachEngine3D
  Height = 14.5
  Placement = pos=(-43.6,-13.8,-18) rot=(0,0,1;0rad)
  Radius = 0.8
FEATURE [Part::Box] Box044  label="Cube042"
  AttacherType = Attacher::AttachEngine3D
  Height = 4
  Length = 12
  Placement = pos=(-50,-16.75,-17) rot=(0,0,1;0rad)
  Width = 26.75
FEATURE [Part::Chamfer] Chamfer001
  Base = -> Box044
  Edges = 1 edges r=7: [Edge3]
FEATURE [Part::Cone] Cone002
  Angle = 360
  AttacherType = Attacher::AttachEngine3D
  Height = 1.5
  Placement = pos=(-43.6,-2.4,-13) rot=(0,0,1;0rad)
  Radius1 = 2.75
  Radius2 = 1.25
FEATURE [Part::Cone] Cone003
  Angle = 360
  AttacherType = Attacher::AttachEngine3D
  Height = 1.5
  Placement = pos=(-43.6,-13.8,-13) rot=(0,0,1;0rad)
  Radius1 = 2.75
  Radius2 = 1.25
FEATURE [Part::Fuse] Fusion114
  Base = -> Cone002
  Tool = -> Cone003
FEATURE [Part::Fuse] Fusion115
  Base = -> Chamfer001
  Tool = -> Fusion114
FEATURE [Part::Fuse] Fusion116
  Base = -> Cylinder081
  Tool = -> Cylinder082
FEATURE [Part::Cut] Cut045028
  Base = -> Fusion115
  Tool = -> Fusion116
FEATURE [Part::Mirroring] Part__Mirroring005  label="Cut045028 (Mirror #6)"
  Base = (0,0,0)
  Normal = (1,0,0)
  Placement = pos=(27,0,0) rot=(0,0,1;0rad)
  Source = -> Cut045028
FEATURE [App::DocumentObjectGroup] Group  label="Older version parts"
  Group = -> [Compound,Compound001,Compound002,Cylinder064,Cylinder010,Cylinder011,Fusion096,Part__Mirroring,Fusion054,Part__Mirroring004,Cut014,Cut015,Cut016,Cut017,Box012,Box013,Box010,Part__Mirroring005,Part__Mirroring003]
FEATURE [Part::Box] Box045  label="Cube043"
  AttacherType = Attacher::AttachEngine3D
  Height = 5
  Length = 2
  Placement = pos=(28,-9,-2) rot=(0,0,1;0rad)
  Width = 12
FEATURE [Part::Box] Box046  label="Cube044"
  AttacherType = Attacher::AttachEngine3D
  Height = 5
  Length = 2
  Placement = pos=(18.5,-9,46) rot=(0,0,1;0rad)
  Width = 12
FEATURE [Part::Box] Box047  label="Cube045"
  AttacherType = Attacher::AttachEngine3D
  Height = 5
  Length = 2
  Placement = pos=(-2,-9,46) rot=(0,0,1;0rad)
  Width = 12
FEATURE [Part::Box] Box048  label="Cube046"
  AttacherType = Attacher::AttachEngine3D
  Height = 5
  Length = 2
  Placement = pos=(37.5,-9,46) rot=(0,0,1;0rad)
  Width = 12
FEATURE [Part::Box] Box049  label="Cube047"
  AttacherType = Attacher::AttachEngine3D
  Height = 5
  Length = 2
  Placement = pos=(8,-9,-2) rot=(0,0,1;0rad)
  Width = 12
FEATURE [Part::Box] Box050  label="Motor Mount Left001"
  AttacherType = Attacher::AttachEngine3D
  Height = 16
  Length = 4
  Placement = pos=(69,-13,7) rot=(0,0,1;0rad)
  Width = 20
FEATURE [Part::Box] Box051  label="Motor Mount Right001"
  AttacherType = Attacher::AttachEngine3D
  Height = 16
  Length = 4
  Placement = pos=(-46,-13,7) rot=(0,0,1;0rad)
  Width = 20
FEATURE [Part::Box] Box052  label="Motor Support Right001"
  AttacherType = Attacher::AttachEngine3D
  Height = 16
  Length = 10
  Placement = pos=(-25,-1,7) rot=(0,0,1;0rad)
  Width = 8
FEATURE [Part::Box] Box053  label="Motor Support Left001"
  AttacherType = Attacher::AttachEngine3D
  Height = 16
  Length = 10
  Placement = pos=(43,-1,7) rot=(0,0,1;0rad)
  Width = 8
FEATURE [Part::Box] Box054  label="Cube014 Arduino Support cube001"
  AttacherType = Attacher::AttachEngine3D
  Height = 67
  Length = 55
  Placement = pos=(-13,5,-68) rot=(0,0,1;0rad)
  Width = 5
FEATURE [Part::Box] Box055  label="Cube048"
  AttacherType = Attacher::AttachEngine3D
  Height = 117
  Length = 33
  Placement = pos=(-46,7,-68) rot=(0,0,1;0rad)
  Width = 3
FEATURE [Part::Box] Box056  label="Cube049"
  AttacherType = Attacher::AttachEngine3D
  Height = 117
  Length = 31
  Placement = pos=(42,7,-68) rot=(0,0,1;0rad)
  Width = 3
FEATURE [Part::Cylinder] Cylinder083  label="Cylinder179"
  Angle = 360
  AttacherType = Attacher::AttachEngine3D
  Height = 28
  Placement = pos=(48,20,-10) rot=(1,0,0;1.5708rad)
  Radius = 1.6
FEATURE [Part::Cylinder] Cylinder084  label="Cylinder180"
  Angle = 360
  AttacherType = Attacher::AttachEngine3D
  Height = 28
  Placement = pos=(48,20,-17) rot=(1,0,0;1.5708rad)
  Radius = 1.6
FEATURE [Part::Cylinder] Cylinder085  label="Cylinder181"
  Angle = 360
  AttacherType = Attacher::AttachEngine3D
  Height = 28
  Placement = pos=(55,20,-17) rot=(1,0,0;1.5708rad)
  Radius = 1.6
FEATURE [Part::Cylinder] Cylinder086  label="Cylinder182"
  Angle = 360
  AttacherType = Attacher::AttachEngine3D
  Height = 28
  Placement = pos=(55,20,-10) rot=(1,0,0;1.5708rad)
  Radius = 1.6
FEATURE [Part::MultiFuse] Fusion117  label="Mount holes top left001"
  Placement = pos=(-1,0,46) rot=(0,0,1;0rad)
  Shapes = -> [Cylinder084,Cylinder085,Cylinder086,Cylinder083]
FEATURE [Part::MultiFuse] Fusion118  label="Mount holes top right001"
  Placement = pos=(-71,0,46) rot=(0,0,1;0rad)
  Shapes = -> [Cylinder084,Cylinder085,Cylinder086,Cylinder083]
FEATURE [Part::Cylinder] Cylinder087  label="Cylinder183"
  Angle = 360
  AttacherType = Attacher::AttachEngine3D
  Height = 10
  Placement = pos=(0,18,29) rot=(0,0,1;0rad)
  Radius = 2.25
FEATURE [Part::Cylinder] Cylinder088  label="Cylinder184"
  Angle = 360
  AttacherType = Attacher::AttachEngine3D
  Height = 10
  Placement = pos=(4.5,18,32) rot=(0,0,1;0rad)
  Radius = 1
FEATURE [Part::Cylinder] Cylinder089  label="Cylinder185"
  Angle = 360
  AttacherType = Attacher::AttachEngine3D
  Height = 10
  Placement = pos=(-4.5,18,32) rot=(0,0,1;0rad)
  Radius = 1
FEATURE [Part::Fuse] Fusion119  label="Mounting Screw Holes002"
  Base = -> Cylinder088
  Tool = -> Cylinder089
FEATURE [Part::Fuse] Fusion120  label="Motor Holes Left001"
  Base = -> Cylinder087
  Placement = pos=(37,-7,-3) rot=(0.57735,0.57735,0.57735;2.0944rad)
  Tool = -> Fusion119
FEATURE [Part::Cylinder] Cylinder090  label="Cylinder186"
  Angle = 360
  AttacherType = Attacher::AttachEngine3D
  Height = 10
  Placement = pos=(0,18,29) rot=(0,0,1;0rad)
  Radius = 2.25
FEATURE [Part::Cylinder] Cylinder091  label="Cylinder187"
  Angle = 360
  AttacherType = Attacher::AttachEngine3D
  Height = 10
  Placement = pos=(4.5,18,32) rot=(0,0,1;0rad)
  Radius = 1
FEATURE [Part::Cylinder] Cylinder092  label="Cylinder188"
  Angle = 360
  AttacherType = Attacher::AttachEngine3D
  Height = 10
  Placement = pos=(-4.5,18,32) rot=(0,0,1;0rad)
  Radius = 1
FEATURE [Part::Fuse] Fusion121  label="Mounting Screw Holes003"
  Base = -> Cylinder091
  Tool = -> Cylinder092
FEATURE [Part::Fuse] Fusion122  label="Motor Holes Right001"
  Base = -> Cylinder090
  Placement = pos=(-79,-7,-3) rot=(0.57735,0.57735,0.57735;2.0944rad)
  Tool = -> Fusion121
FEATURE [Part::Cylinder] Cylinder093  label="Cylinder189"
  Angle = 360
  AttacherType = Attacher::AttachEngine3D
  Height = 28
  Placement = pos=(40.7,0,-10.3) rot=(1,0,0;1.5708rad)
  Radius = 1.6
FEATURE [Part::Cylinder] Cylinder094  label="Cylinder190"
  Angle = 360
  AttacherType = Attacher::AttachEngine3D
  Height = 28
  Placement = pos=(-2.4,0,-59.8) rot=(1,0,0;1.5708rad)
  Radius = 1.6
FEATURE [Part::Cylinder] Cylinder095  label="Cylinder191"
  Angle = 360
  AttacherType = Attacher::AttachEngine3D
  Height = 28
  Placement = pos=(-5,0,-9) rot=(1,0,0;1.5708rad)
  Radius = 1.6
FEATURE [Part::Cylinder] Cylinder096  label="Cylinder192"
  Angle = 360
  AttacherType = Attacher::AttachEngine3D
  Height = 28
  Placement = pos=(25.5,0,-59.8) rot=(1,0,0;1.5708rad)
  Radius = 1.6
FEATURE [Part::Fuse] Fusion123
  Base = -> Cylinder094
  Tool = -> Cylinder095
FEATURE [Part::Fuse] Fusion124
  Base = -> Cylinder093
  Tool = -> Cylinder096
FEATURE [Part::Fuse] Fusion125  label="Screw holes on Arduino Duo002"
  Base = -> Fusion123
  Tool = -> Fusion124
FEATURE [Part::Mirroring] Part__Mirroring006  label="Screw holes on Arduino Duo (Mirror #1)002"
  Base = (0,0,0)
  Normal = (0,0,1)
  Placement = pos=(-4,10,-67) rot=(0,0,1;0rad)
  Source = -> Fusion125
FEATURE [Part::Mirroring] Part__Mirroring007  label="Screw holes on Arduino Duo (Mirror #1)001 (Mirror #4)001"
  Base = (0,0,0)
  Normal = (1,0,0)
  Placement = pos=(27,0,-6) rot=(0,0,1;0rad)
  Source = -> Part__Mirroring006
FEATURE [Part::Box] Box057  label="Cube050"
  AttacherType = Attacher::AttachEngine3D
  Height = 50
  Length = 47
  Placement = pos=(-9,-8,0) rot=(0,0,1;0rad)
  Width = 12
FEATURE [Part::Box] Box058  label="Cube051"
  AttacherType = Attacher::AttachEngine3D
  Height = 55
  Length = 53
  Placement = pos=(-12,-8,-2.5) rot=(0,0,1;0rad)
  Width = 11
FEATURE [Part::Cut] Cut045029
  Base = -> Box058
  Tool = -> Box057
FEATURE [Part::Box] Box059  label="Cube052"
  AttacherType = Attacher::AttachEngine3D
  Height = 5
  Length = 3
  Placement = pos=(35,-9,-4) rot=(0,0,1;0rad)
  Width = 12
FEATURE [Part::Cut] Cut045030
  Base = -> Cut045029
  Placement = pos=(-9,10,-58) rot=(1,0,0;1.5708rad)
  Tool = -> Box059
FEATURE [Part::Cut] Cut045031
  Base = -> Cut045029
  Placement = pos=(36.7,10,-56.7) rot=(1,0,0;1.5708rad)
  Tool = -> Box059
FEATURE [Part::Cut] Cut045032
  Base = -> Cut045029
  Placement = pos=(-6.4,10,-7.2) rot=(1,0,0;1.5708rad)
  Tool = -> Box059
FEATURE [Part::Cut] Cut045033
  Base = -> Cut045029
  Placement = pos=(21.5,10,-7.2) rot=(1,0,0;1.5708rad)
  Tool = -> Box059
FEATURE [Part::MultiFuse] Fusion126
  Shapes = -> [Cut045030,Cut045033,Cut045031,Cut045032]
FEATURE [Part::Mirroring] Part__Mirroring008  label="Hex Holes001"
  Base = (0,0,0)
  Normal = (1,0,0)
  Placement = pos=(27,0,-6) rot=(0,0,1;0rad)
  Source = -> Fusion126
FEATURE [Part::Box] Box060  label="Cube053"
  AttacherType = Attacher::AttachEngine3D
  Height = 5
  Length = 2
  Placement = pos=(37.5,-9,-2) rot=(0,0,1;0rad)
  Width = 12
FEATURE [Part::Box] Box061  label="Battery Base001"
  AttacherType = Attacher::AttachEngine3D
  Height = 50
  Length = 55
  Placement = pos=(-13,3,-1) rot=(0,0,1;0rad)
  Width = 7
FEATURE [Part::Cylinder] Cylinder097  label="Cylinder193"
  Angle = 360
  AttacherType = Attacher::AttachEngine3D
  Height = 42
  Radius = 4.8
FEATURE [Part::Cylinder] Cylinder098  label="Cylinder194"
  Angle = 360
  AttacherType = Attacher::AttachEngine3D
  Height = 1.6
  Placement = pos=(0,0,42) rot=(0,0,1;0rad)
  Radius = 1.65
FEATURE [Part::Fuse] Fusion127
  Base = -> Cylinder097
  Placement = pos=(2,0,0) rot=(0,0,1;0rad)
  Tool = -> Cylinder098
FEATURE [Part::Cylinder] Cylinder099  label="Cylinder195"
  Angle = 360
  AttacherType = Attacher::AttachEngine3D
  Height = 42
  Radius = 4.8
FEATURE [Part::Cylinder] Cylinder100  label="Cylinder196"
  Angle = 360
  AttacherType = Attacher::AttachEngine3D
  Height = 1.6
  Placement = pos=(0,0,42) rot=(0,0,1;0rad)
  Radius = 1.65
FEATURE [Part::Fuse] Fusion128
  Base = -> Cylinder099
  Placement = pos=(12,0,0) rot=(0,0,1;0rad)
  Tool = -> Cylinder100
FEATURE [Part::Cylinder] Cylinder101  label="Cylinder197"
  Angle = 360
  AttacherType = Attacher::AttachEngine3D
  Height = 42
  Radius = 4.8
FEATURE [Part::Cylinder] Cylinder102  label="Cylinder198"
  Angle = 360
  AttacherType = Attacher::AttachEngine3D
  Height = 1.6
  Placement = pos=(0,0,42) rot=(0,0,1;0rad)
  Radius = 1.65
FEATURE [Part::Fuse] Fusion129
  Base = -> Cylinder101
  Placement = pos=(22,0,0) rot=(0,0,1;0rad)
  Tool = -> Cylinder102
FEATURE [Part::Cylinder] Cylinder103  label="Cylinder199"
  Angle = 360
  AttacherType = Attacher::AttachEngine3D
  Height = 42
  Radius = 4.8
FEATURE [Part::Cylinder] Cylinder104  label="Cylinder200"
  Angle = 360
  AttacherType = Attacher::AttachEngine3D
  Height = 1.6
  Placement = pos=(0,0,42) rot=(0,0,1;0rad)
  Radius = 1.65
FEATURE [Part::Fuse] Fusion130
  Base = -> Cylinder103
  Placement = pos=(32,0,0) rot=(0,0,1;0rad)
  Tool = -> Cylinder104
FEATURE [Part::Cylinder] Cylinder105  label="Cylinder201"
  Angle = 360
  AttacherType = Attacher::AttachEngine3D
  Height = 42
  Radius = 4.8
FEATURE [Part::Cylinder] Cylinder106  label="Cylinder202"
  Angle = 360
  AttacherType = Attacher::AttachEngine3D
  Height = 1.6
  Placement = pos=(0,0,42) rot=(0,0,1;0rad)
  Radius = 1.65
FEATURE [Part::Fuse] Fusion131
  Base = -> Cylinder105
  Placement = pos=(-8,0,0) rot=(0,0,1;0rad)
  Tool = -> Cylinder106
FEATURE [Part::MultiFuse] Fusion132  label="AAA Batts002"
  Placement = pos=(2,0,2) rot=(0,0,1;0rad)
  Shapes = -> [Fusion131,Fusion127,Fusion128,Fusion129,Fusion130]
FEATURE [Part::Cut] Cut045034
  Base = -> Box061
  Tool = -> Fusion132
FEATURE [Part::Box] Box062  label="Cube054"
  AttacherType = Attacher::AttachEngine3D
  Height = 2.5
  Length = 55
  Placement = pos=(-13,-9,-1) rot=(0,0,1;0rad)
  Width = 12
FEATURE [Part::Box] Box063  label="Cube055"
  AttacherType = Attacher::AttachEngine3D
  Height = 2.5
  Length = 55
  Placement = pos=(-13,-9,46.5) rot=(0,0,1;0rad)
  Width = 12
FEATURE [Part::Box] Box064  label="Cube056"
  AttacherType = Attacher::AttachEngine3D
  Height = 50
  Length = 2.5
  Placement = pos=(-13,-9,-1) rot=(0,0,1;0rad)
  Width = 12
FEATURE [Part::Box] Box065  label="Cube057"
  AttacherType = Attacher::AttachEngine3D
  Height = 50
  Length = 2.5
  Placement = pos=(39.5,-9,-1) rot=(0,0,1;0rad)
  Width = 12
FEATURE [Part::MultiFuse] Fusion133
  Shapes = -> [Box062,Box064,Box065,Box063]
FEATURE [Part::Box] Box066  label="Cube058"
  AttacherType = Attacher::AttachEngine3D
  Height = 5
  Length = 2
  Placement = pos=(-10.5,-9,46) rot=(0,0,1;0rad)
  Width = 12
FEATURE [Part::Box] Box067  label="Cube059"
  AttacherType = Attacher::AttachEngine3D
  Height = 5
  Length = 2
  Placement = pos=(-10.5,-9,-2) rot=(0,0,1;0rad)
  Width = 12
FEATURE [Part::MultiFuse] Fusion134
  Shapes = -> [Box067,Box066,Box060,Box048]
FEATURE [Part::MultiFuse] Fusion135
  Shapes = -> [Box045,Box046,Box047,Box049]
FEATURE [Part::Cut] Cut045035
  Base = -> Fusion133
  Tool = -> Fusion134
FEATURE [Part::Cut] Cut045036
  Base = -> Cut045035
  Tool = -> Fusion135
FEATURE [Part::Cylinder] Cylinder107  label="Cylinder203"
  Angle = 360
  AttacherType = Attacher::AttachEngine3D
  Height = 14.5
  Placement = pos=(-43.6,-2.4,-15) rot=(0,0,1;0rad)
  Radius = 0.8
FEATURE [Part::Cylinder] Cylinder108  label="Cylinder204"
  Angle = 360
  AttacherType = Attacher::AttachEngine3D
  Height = 14.5
  Placement = pos=(-43.6,-13.8,-15) rot=(0,0,1;0rad)
  Radius = 0.8
FEATURE [Part::Fuse] Fusion136
  Base = -> Cut045034
  Tool = -> Cut045036
FEATURE [Part::Box] Box068  label="Cube060"
  AttacherType = Attacher::AttachEngine3D
  Height = 4
  Length = 12
  Placement = pos=(-50,-16.75,-14) rot=(0,0,1;0rad)
  Width = 26.75
FEATURE [Part::Chamfer] Chamfer002
  Base = -> Box068
  Edges = 1 edges r=7: [Edge3]
FEATURE [Part::Cone] Cone004
  Angle = 360
  AttacherType = Attacher::AttachEngine3D
  Height = 1.5
  Placement = pos=(-43.6,-2.4,-10) rot=(0,0,1;0rad)
  Radius1 = 2.75
  Radius2 = 1.25
FEATURE [Part::Cone] Cone005
  Angle = 360
  AttacherType = Attacher::AttachEngine3D
  Height = 1.5
  Placement = pos=(-43.6,-13.8,-10) rot=(0,0,1;0rad)
  Radius1 = 2.75
  Radius2 = 1.25
FEATURE [Part::Fuse] Fusion137
  Base = -> Cone004
  Tool = -> Cone005
FEATURE [Part::Fuse] Fusion138
  Base = -> Chamfer002
  Tool = -> Fusion137
FEATURE [Part::Fuse] Fusion139
  Base = -> Cylinder107
  Tool = -> Cylinder108
FEATURE [Part::Cut] Cut045037
  Base = -> Fusion138
  Tool = -> Fusion139
FEATURE [Part::Cylinder] Cylinder109  label="Cylinder205"
  Angle = 360
  AttacherType = Attacher::AttachEngine3D
  Height = 14.5
  Placement = pos=(-43.6,-2.4,-15) rot=(0,0,1;0rad)
  Radius = 0.8
FEATURE [Part::Cylinder] Cylinder110  label="Cylinder206"
  Angle = 360
  AttacherType = Attacher::AttachEngine3D
  Height = 14.5
  Placement = pos=(-43.6,-13.8,-15) rot=(0,0,1;0rad)
  Radius = 0.8
FEATURE [Part::Box] Box069  label="Cube061"
  AttacherType = Attacher::AttachEngine3D
  Height = 4
  Length = 12
  Placement = pos=(-50,-16.75,-14) rot=(0,0,1;0rad)
  Width = 26.75
FEATURE [Part::Chamfer] Chamfer003
  Base = -> Box069
  Edges = 1 edges r=7: [Edge3]
FEATURE [Part::Cone] Cone006
  Angle = 360
  AttacherType = Attacher::AttachEngine3D
  Height = 1.5
  Placement = pos=(-43.6,-2.4,-10) rot=(0,0,1;0rad)
  Radius1 = 2.75
  Radius2 = 1.25
FEATURE [Part::Cone] Cone007
  Angle = 360
  AttacherType = Attacher::AttachEngine3D
  Height = 1.5
  Placement = pos=(-43.6,-13.8,-10) rot=(0,0,1;0rad)
  Radius1 = 2.75
  Radius2 = 1.25
FEATURE [Part::Fuse] Fusion140
  Base = -> Cone006
  Tool = -> Cone007
FEATURE [Part::Fuse] Fusion141
  Base = -> Chamfer003
  Tool = -> Fusion140
FEATURE [Part::Fuse] Fusion142
  Base = -> Cylinder109
  Tool = -> Cylinder110
FEATURE [Part::Cut] Cut045038
  Base = -> Fusion141
  Tool = -> Fusion142
FEATURE [Part::Mirroring] Part__Mirroring009  label="Cut045028 (Mirror #6)001"
  Base = (0,0,0)
  Normal = (1,0,0)
  Placement = pos=(27,0,0) rot=(0,0,1;0rad)
  Source = -> Cut045038
FEATURE [Part::Cut] Cut045039
  Base = -> Box050
  Tool = -> Fusion120
FEATURE [Part::Cut] Cut045040
  Base = -> Box051
  Tool = -> Fusion122
FEATURE [Part::MultiFuse] Fusion143
  Shapes = -> [Box054,Box055,Box056]
FEATURE [Part::Fuse] Fusion144
  Base = -> Fusion136
  Tool = -> Fusion143
FEATURE [Part::MultiFuse] Fusion145
  Shapes = -> [Fusion144,Cut045040,Cut045039]
FEATURE [Part::MultiFuse] Fusion146
  Shapes = -> [Fusion145,Part__Mirroring009,Cut045037]
FEATURE [Part::Cut] Cut045041
  Base = -> Fusion146
  Tool = -> Fusion117
FEATURE [Part::Cut] Cut045042
  Base = -> Cut045041
  Tool = -> Fusion118
FEATURE [Part::Cut] Cut045043
  Base = -> Cut045042
  Tool = -> Part__Mirroring007
FEATURE [Part::Cut] Cut045044
  Base = -> Cut045043
  Tool = -> Part__Mirroring008
FEATURE [Part::MultiFuse] Fusion147
  Shapes = -> [Cut045044,Box053,Box052]
FEATURE [Part::Chamfer] Chamfer004
  Base = -> Fusion147
  Edges = 1 edges r=25: [Edge43]
FEATURE [Part::Chamfer] Chamfer005
  Base = -> Chamfer004
  Edges = 1 edges r=25: [Edge225]
FEATURE [Part::Chamfer] Chamfer006
  Base = -> Chamfer005
  Edges = 1 edges r=30: [Edge58]
FEATURE [Part::Chamfer] Chamfer007
  Base = -> Chamfer006
  Edges = 1 edges r=30: [Edge148]
FEATURE [Part::Fillet] Fillet
  Base = -> Chamfer007
  Edges = 1 edges r=2: [Edge233]
FEATURE [Part::Fillet] Fillet001
  Base = -> Fillet
  Edges = 1 edges r=2: [Edge6]
FEATURE [Part::Fillet] Fillet002
  Base = -> Fillet001
  Edges = 1 edges r=2: [Edge2]
FEATURE [Part::Fillet] Fillet003
  Base = -> Fillet002
  Edges = 1 edges r=2: [Edge357]
FEATURE [Part::Fillet] Fillet004
  Base = -> Fillet003
  Edges = 1 edges r=2: [Edge6]
FEATURE [Part::Fillet] Fillet005
  Base = -> Fillet004
  Edges = 1 edges r=2: [Edge2]
FEATURE [Part::Fillet] Fillet006
  Base = -> Fillet005
  Edges = 1 edges r=2: [Edge407]
FEATURE [Part::Fillet] Fillet007
  Base = -> Fillet006
  Edges = 1 edges r=2: [Edge2]
FEATURE [Part::Fillet] Fillet008
  Base = -> Fillet007
  Edges = 1 edges r=2: [Edge369]
FEATURE [Part::Fillet] Fillet009
  Base = -> Fillet008
  Edges = 1 edges r=2: [Edge2]
FEATURE [Part::Cylinder] Cylinder111  label="Cylinder207"
  Angle = 360
  AttacherType = Attacher::AttachEngine3D
  Height = 28
  Placement = pos=(45,6,47) rot=(0.707107,0,0.707107;4.01426rad)
  Radius = 0.5
FEATURE [Part::Cylinder] Cylinder112  label="Cylinder208"
  Angle = 360
  AttacherType = Attacher::AttachEngine3D
  Height = 28
  Placement = pos=(66,6,26) rot=(0.707107,0,0.707107;4.01426rad)
  Radius = 0.5
FEATURE [Part::Cut] Cut045045
  Base = -> Fillet009
  Tool = -> Cylinder111
FEATURE [Part::Cut] Cut045046
  Base = -> Cut045045
  Tool = -> Cylinder112
FEATURE [Part::Cylinder] Cylinder113  label="Cylinder209"
  Angle = 360
  AttacherType = Attacher::AttachEngine3D
  Height = 28
  Placement = pos=(66,6,26) rot=(0.707107,0,0.707107;4.01426rad)
  Radius = 0.5
FEATURE [Part::Mirroring] Part__Mirroring010  label="Cylinder137 (Mirror #7)"
  Base = (0,0,0)
  Normal = (1,0,0)
  Placement = pos=(27,0,0) rot=(0,0,1;0rad)
  Source = -> Cylinder113
FEATURE [Part::Cylinder] Cylinder114  label="Cylinder210"
  Angle = 360
  AttacherType = Attacher::AttachEngine3D
  Height = 28
  Placement = pos=(45,6,47) rot=(0.707107,0,0.707107;4.01426rad)
  Radius = 0.5
FEATURE [Part::Mirroring] Part__Mirroring011  label="Cylinder138 (Mirror #8)"
  Base = (0,0,0)
  Normal = (1,0,0)
  Placement = pos=(27,0,0) rot=(0,0,1;0rad)
  Source = -> Cylinder114
FEATURE [Part::Cut] Cut045047
  Base = -> Cut045046
  Tool = -> Part__Mirroring010
FEATURE [Part::Cut] Cut045048  label="Old Layout"
  Base = -> Cut045047
  Tool = -> Part__Mirroring011
FEATURE [Part::Cylinder] Cylinder115  label="Arduino Cylinder191"
  Angle = 360
  AttacherType = Attacher::AttachEngine3D
  Height = 28
  Placement = pos=(4,11,-8.6) rot=(1,0,0;1.5708rad)
  Radius = 1.6
FEATURE [Part::Cylinder] Cylinder116  label="Arduino Cylinder192"
  Angle = 360
  AttacherType = Attacher::AttachEngine3D
  Height = 28
  Placement = pos=(31.9,11,-8.6) rot=(1,0,0;1.5708rad)
  Radius = 1.6
FEATURE [Part::Cylinder] Cylinder117  label="Arduino Cylinder193"
  Angle = 360
  AttacherType = Attacher::AttachEngine3D
  Height = 28
  Placement = pos=(-11.2,11,-59.4) rot=(1,0,0;1.5708rad)
  Radius = 1.6
FEATURE [Part::Cylinder] Cylinder118  label="Arduino Cylinder194"
  Angle = 360
  AttacherType = Attacher::AttachEngine3D
  Height = 28
  Placement = pos=(37.2,11,-60.5) rot=(1,0,0;1.5708rad)
  Radius = 1.6
FEATURE [Part::Cylinder] Cylinder119  label="Arduino Cylinder195"
  Angle = 360
  AttacherType = Attacher::AttachEngine3D
  Height = 2.5
  Placement = pos=(4,13,-8.6) rot=(1,0,0;1.5708rad)
  Radius = 4
FEATURE [Part::Feature] Box014001
  Placement = pos=(3.88157,4,-2.89487) rot=(0,1,0;1.0472rad)
  shape: bbox 13.66 x 10 x 13.66 mm, 6 faces (baked)
FEATURE [Part::Feature] Box014002
  Placement = pos=(8.88157,4,-5.64487) rot=(0,1,0;2.0944rad)
  shape: bbox 13.66 x 10 x 13.66 mm, 6 faces (baked)
FEATURE [Part::Feature] Box014003
  Placement = pos=(9,4,-11.35) rot=(0,1,0;3.14159rad)
  shape: bbox 10 x 10 x 10 mm, 6 faces (baked)
FEATURE [Part::Feature] Box014004
  Placement = pos=(4.11843,4,-14.3051) rot=(0,1,0;4.18879rad)
  shape: bbox 13.66 x 10 x 13.66 mm, 6 faces (baked)
FEATURE [Part::Feature] Box014005
  Placement = pos=(-0.88157,4,-11.5551) rot=(0,-1,0;1.0472rad)
  shape: bbox 13.66 x 10 x 13.66 mm, 6 faces (baked)
FEATURE [Part::MultiFuse] Fusion148
  Shapes = -> [Box014001,Box014002,Box014004,Box014003,Box014005,Box014]
FEATURE [Part::Cut] Cut045049  label="M3 Nut004"
  Base = -> Cylinder119
  Placement = pos=(0,-3,0) rot=(0,0,1;0rad)
  Tool = -> Fusion148
FEATURE [Part::Box] Box014006  label="Not used Cube001"
  AttacherType = Attacher::AttachEngine3D
  Height = 10
  Length = 10
  Placement = pos=(-1,4,-5.85) rot=(0,0,1;0rad)
  Width = 10
FEATURE [Part::Cylinder] Cylinder120  label="Arduino Cylinder196"
  Angle = 360
  AttacherType = Attacher::AttachEngine3D
  Height = 2.5
  Placement = pos=(4,13,-8.6) rot=(1,0,0;1.5708rad)
  Radius = 4
FEATURE [Part::Feature] Box014007
  Placement = pos=(3.88157,4,-2.89487) rot=(0,1,0;1.0472rad)
  shape: bbox 13.66 x 10 x 13.66 mm, 6 faces (baked)
FEATURE [Part::Feature] Box014008
  Placement = pos=(8.88157,4,-5.64487) rot=(0,1,0;2.0944rad)
  shape: bbox 13.66 x 10 x 13.66 mm, 6 faces (baked)
FEATURE [Part::Feature] Box014009
  Placement = pos=(9,4,-11.35) rot=(0,1,0;3.14159rad)
  shape: bbox 10 x 10 x 10 mm, 6 faces (baked)
FEATURE [Part::Feature] Box014010
  Placement = pos=(4.11843,4,-14.3051) rot=(0,1,0;4.18879rad)
  shape: bbox 13.66 x 10 x 13.66 mm, 6 faces (baked)
FEATURE [Part::Feature] Box014011
  Placement = pos=(-0.88157,4,-11.5551) rot=(0,-1,0;1.0472rad)
  shape: bbox 13.66 x 10 x 13.66 mm, 6 faces (baked)
FEATURE [Part::MultiFuse] Fusion149
  Shapes = -> [Box014007,Box014008,Box014010,Box014009,Box014011,Box014006]
FEATURE [Part::Cut] Cut045050  label="M3 Nut005"
  Base = -> Cylinder120
  Placement = pos=(27.9,-3,0) rot=(0,0,1;0rad)
  Tool = -> Fusion149
FEATURE [Part::Box] Box014012  label="Not used Cube002"
  AttacherType = Attacher::AttachEngine3D
  Height = 10
  Length = 10
  Placement = pos=(-1,4,-5.85) rot=(0,0,1;0rad)
  Width = 10
FEATURE [Part::Cylinder] Cylinder121  label="Arduino Cylinder197"
  Angle = 360
  AttacherType = Attacher::AttachEngine3D
  Height = 2.5
  Placement = pos=(4,13,-8.6) rot=(1,0,0;1.5708rad)
  Radius = 4
FEATURE [Part::Feature] Box014013
  Placement = pos=(3.88157,4,-2.89487) rot=(0,1,0;1.0472rad)
  shape: bbox 13.66 x 10 x 13.66 mm, 6 faces (baked)
FEATURE [Part::Feature] Box014014
  Placement = pos=(8.88157,4,-5.64487) rot=(0,1,0;2.0944rad)
  shape: bbox 13.66 x 10 x 13.66 mm, 6 faces (baked)
FEATURE [Part::Feature] Box014015
  Placement = pos=(9,4,-11.35) rot=(0,1,0;3.14159rad)
  shape: bbox 10 x 10 x 10 mm, 6 faces (baked)
FEATURE [Part::Feature] Box014016
  Placement = pos=(4.11843,4,-14.3051) rot=(0,1,0;4.18879rad)
  shape: bbox 13.66 x 10 x 13.66 mm, 6 faces (baked)
FEATURE [Part::Feature] Box014017
  Placement = pos=(-0.88157,4,-11.5551) rot=(0,-1,0;1.0472rad)
  shape: bbox 13.66 x 10 x 13.66 mm, 6 faces (baked)
FEATURE [Part::MultiFuse] Fusion150
  Shapes = -> [Box014013,Box014014,Box014016,Box014015,Box014017,Box014012]
FEATURE [Part::Cut] Cut045051  label="M3 Nut006"
  Base = -> Cylinder121
  Placement = pos=(-15.2,-3,-50.8) rot=(0,0,1;0rad)
  Tool = -> Fusion150
FEATURE [Part::Box] Box014018  label="Not used Cube003"
  AttacherType = Attacher::AttachEngine3D
  Height = 10
  Length = 10
  Placement = pos=(-1,4,-5.85) rot=(0,0,1;0rad)
  Width = 10
FEATURE [Part::Cylinder] Cylinder122  label="Arduino Cylinder198"
  Angle = 360
  AttacherType = Attacher::AttachEngine3D
  Height = 2.5
  Placement = pos=(4,13,-8.6) rot=(1,0,0;1.5708rad)
  Radius = 4
FEATURE [Part::Feature] Box014019
  Placement = pos=(3.88157,4,-2.89487) rot=(0,1,0;1.0472rad)
  shape: bbox 13.66 x 10 x 13.66 mm, 6 faces (baked)
FEATURE [Part::Feature] Box014020
  Placement = pos=(8.88157,4,-5.64487) rot=(0,1,0;2.0944rad)
  shape: bbox 13.66 x 10 x 13.66 mm, 6 faces (baked)
FEATURE [Part::Feature] Box014021
  Placement = pos=(9,4,-11.35) rot=(0,1,0;3.14159rad)
  shape: bbox 10 x 10 x 10 mm, 6 faces (baked)
FEATURE [Part::Feature] Box014022
  Placement = pos=(4.11843,4,-14.3051) rot=(0,1,0;4.18879rad)
  shape: bbox 13.66 x 10 x 13.66 mm, 6 faces (baked)
FEATURE [Part::Feature] Box014023
  Placement = pos=(-0.88157,4,-11.5551) rot=(0,-1,0;1.0472rad)
  shape: bbox 13.66 x 10 x 13.66 mm, 6 faces (baked)
FEATURE [Part::MultiFuse] Fusion151
  Shapes = -> [Box014019,Box014020,Box014022,Box014021,Box014023,Box014018]
FEATURE [Part::Cut] Cut045052  label="M3 Nut007"
  Base = -> Cylinder122
  Placement = pos=(33.2,-3,-51.9) rot=(0,0,1;0rad)
  Tool = -> Fusion151
FEATURE [Part::Box] Box014024  label="Cube062"
  AttacherType = Attacher::AttachEngine3D
  Height = 67
  Length = 65
  Placement = pos=(-16,-13,-6) rot=(0,0,1;0rad)
  Width = 8
FEATURE [Part::Cut] Cut045053  label="BAtt Holder"
  Base = -> Fusion110
  Tool = -> Box014024
FEATURE [Part::Cylinder] Cylinder123  label="Cylinder211"
  Angle = 360
  AttacherType = Attacher::AttachEngine3D
  Height = 28
  Placement = pos=(45,6,47) rot=(0.707107,0,0.707107;4.01426rad)
  Radius = 0.5
FEATURE [Part::Cylinder] Cylinder124  label="Cylinder212"
  Angle = 360
  AttacherType = Attacher::AttachEngine3D
  Height = 28
  Placement = pos=(66,6,26) rot=(0.707107,0,0.707107;4.01426rad)
  Radius = 0.5
FEATURE [Part::Cylinder] Cylinder125  label="Cylinder213"
  Angle = 360
  AttacherType = Attacher::AttachEngine3D
  Height = 28
  Placement = pos=(45,6,47) rot=(0.707107,0,0.707107;4.01426rad)
  Radius = 0.5
FEATURE [Part::Cylinder] Cylinder126  label="Cylinder214"
  Angle = 360
  AttacherType = Attacher::AttachEngine3D
  Height = 28
  Placement = pos=(66,6,26) rot=(0.707107,0,0.707107;4.01426rad)
  Radius = 0.5
FEATURE [Part::Mirroring] Part__Mirroring012  label="Cylinder211 (Mirror #13)"
  Base = (0,0,0)
  Normal = (1,0,0)
  Placement = pos=(27,0,0) rot=(0,0,1;0rad)
  Source = -> Cylinder125
FEATURE [Part::Mirroring] Part__Mirroring013  label="Cylinder212 (Mirror #14)"
  Base = (0,0,0)
  Normal = (1,0,0)
  Placement = pos=(27,0,0) rot=(0,0,1;0rad)
  Source = -> Cylinder126
FEATURE [Part::Box] Box014025  label="Cube063"
  AttacherType = Attacher::AttachEngine3D
  Height = 14
  Length = 15
  Placement = pos=(-46,4,-27) rot=(0,0,1;0rad)
  Width = 3
FEATURE [Part::Cylinder] Cylinder127  label="Cylinder215"
  Angle = 360
  AttacherType = Attacher::AttachEngine3D
  Height = 10
  Placement = pos=(-39,9,-22) rot=(1,0,0;1.5708rad)
  Radius = 3
FEATURE [Part::Box] Box014026  label="Cube064"
  AttacherType = Attacher::AttachEngine3D
  Height = 9.5
  Length = 15
  Placement = pos=(-46,0,-27) rot=(0,0,1;0rad)
  Width = 3
FEATURE [Part::Cylinder] Cylinder128  label="Cylinder216"
  Angle = 360
  AttacherType = Attacher::AttachEngine3D
  Height = 14
  Placement = pos=(-39,11,-22) rot=(1,0,0;1.5708rad)
  Radius = 1.5
FEATURE [Part::Cut] Cut045054
  Base = -> Box014025
  Tool = -> Cylinder127
FEATURE [Part::Cylinder] Cylinder129  label="Cylinder217"
  Angle = 360
  AttacherType = Attacher::AttachEngine3D
  Height = 14
  Placement = pos=(-39,11,-22) rot=(1,0,0;1.5708rad)
  Radius = 1.5
FEATURE [Part::Cut] Cut045055  label="Printed Washer"
  Base = -> Box014026
  Tool = -> Cylinder128
FEATURE [Part::Box] Box014027  label="Cube065"
  AttacherType = Attacher::AttachEngine3D
  Height = 23
  Length = 22
  Placement = pos=(-46,4,0) rot=(0,0,1;0rad)
  Width = 3
FEATURE [Part::Cylinder] Cylinder130  label="Cylinder218"
  Angle = 360
  AttacherType = Attacher::AttachEngine3D
  Height = 14
  Placement = pos=(-38,11,4) rot=(1,0,0;1.5708rad)
  Radius = 1.5
FEATURE [Part::Cylinder] Cylinder131  label="Cylinder219"
  Angle = 360
  AttacherType = Attacher::AttachEngine3D
  Height = 14
  Placement = pos=(-28,11,4) rot=(1,0,0;1.5708rad)
  Radius = 1.5
FEATURE [Part::Cylinder] Cylinder132  label="Cylinder220"
  Angle = 360
  AttacherType = Attacher::AttachEngine3D
  Height = 14.5
  Placement = pos=(-53.76,-13.8,-18) rot=(0,0,1;0rad)
  Radius = 0.8
FEATURE [Part::Box] Box014028  label="Cube066"
  AttacherType = Attacher::AttachEngine3D
  Height = 4
  Length = 19
  Placement = pos=(-57,-16.75,-17) rot=(0,0,1;0rad)
  Width = 8.75
FEATURE [Part::Cone] Cone008
  Angle = 360
  AttacherType = Attacher::AttachEngine3D
  Height = 1.5
  Placement = pos=(-53.76,-13.8,-13) rot=(0,0,1;0rad)
  Radius1 = 2.75
  Radius2 = 1.25
FEATURE [Part::Fuse] Fusion152
  Base = -> Fusion111
  Tool = -> Cone008
FEATURE [Part::Fuse] Fusion153
  Base = -> Fusion113
  Tool = -> Cylinder132
FEATURE [Part::Fuse] Fusion154
  Base = -> Box043
  Tool = -> Box014028
FEATURE [Part::Fuse] Fusion155
  Base = -> Cut045054
  Tool = -> Fusion154
FEATURE [Part::Fuse] Fusion156
  Base = -> Fusion152
  Tool = -> Fusion155
FEATURE [Part::Cut] Cut045056
  Base = -> Fusion156
  Tool = -> Fusion153
FEATURE [Part::Chamfer] Chamfer
  Base = -> Cut045056
  Edges = 1 edges r=6.99: [Edge15]
FEATURE [Part::Fillet] Fillet010
  Base = -> Chamfer
  Edges = 1 edges r=1: [Edge51]
FEATURE [Part::Fillet] Fillet011
  Base = -> Fillet010
  Edges = 1 edges r=1: [Edge11]
FEATURE [Part::Fillet] Fillet012
  Base = -> Fillet011
  Edges = 1 edges r=1: [Edge37]
FEATURE [Part::Fillet] Fillet013
  Base = -> Fillet012
  Edges = 1 edges r=5: [Edge54]
FEATURE [Part::Fillet] Fillet014
  Base = -> Fillet013
  Edges = 1 edges r=5: [Edge12]
FEATURE [Part::Chamfer] Chamfer008
  Base = -> Fusion104
  Edges = 1 edges r=0.5: [Edge77]
FEATURE [Part::Chamfer] Chamfer009
  Base = -> Chamfer008
  Edges = 1 edges r=0.5: [Edge6]
